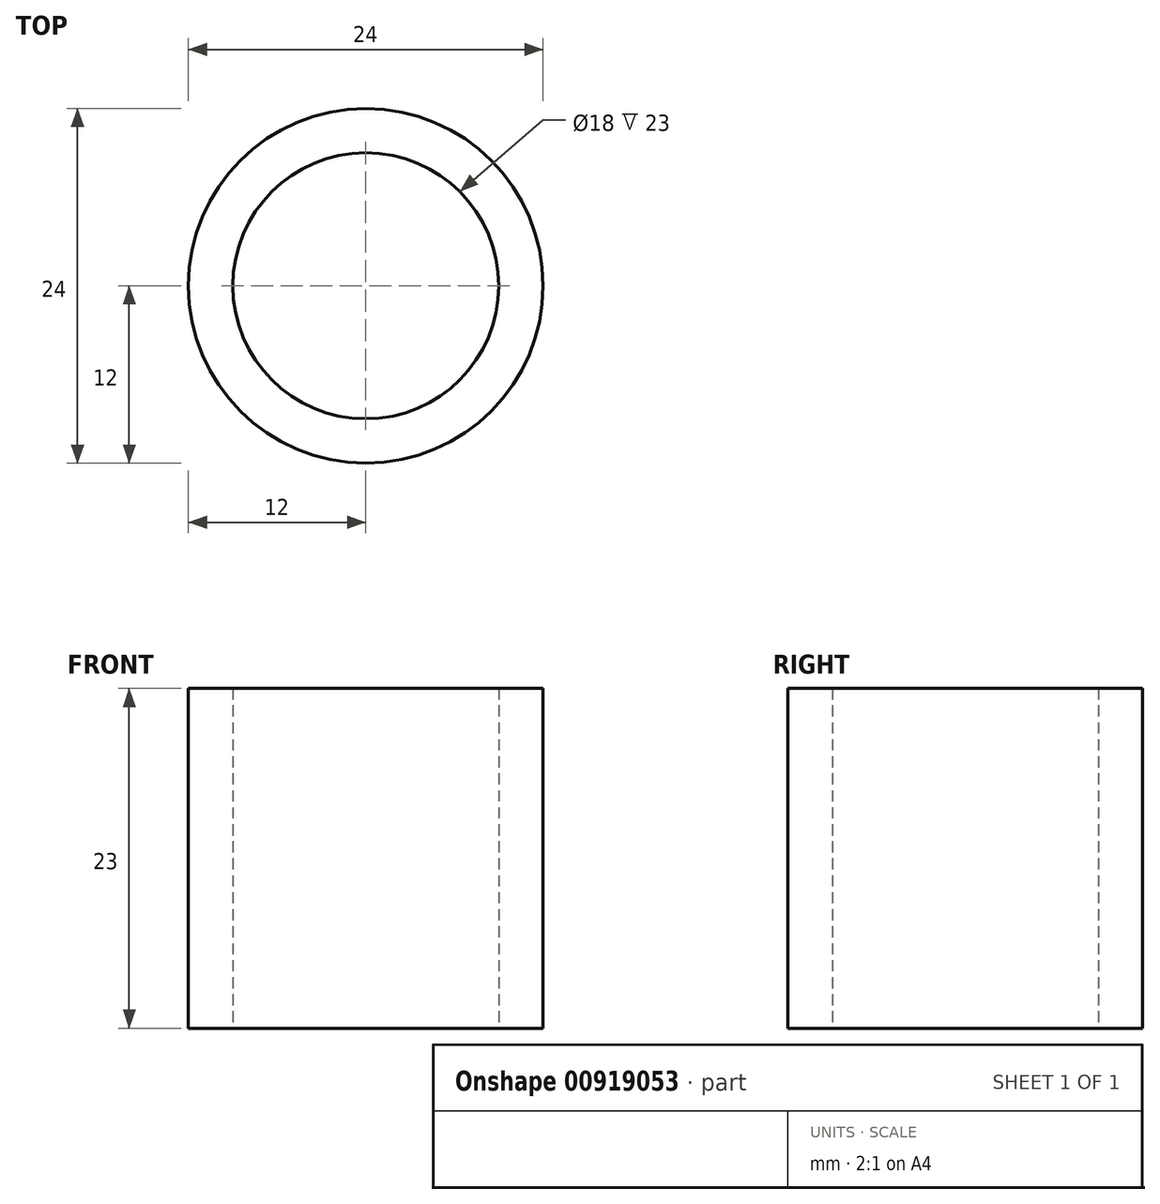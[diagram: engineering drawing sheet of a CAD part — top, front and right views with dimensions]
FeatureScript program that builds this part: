
annotation { "Feature Type Name" : "Feature", "Feature Type Description" : "" }
export const myFeature = defineFeature(function(context is Context, id is Id, definition is map)
    precondition{}
    {
        {
            var Q0;
            Q0=qCreatedBy(makeId("Top.planeOp"),FACE);
            var sketch = newSketch(context, id + "F0", { "sketchPlane" : qUnion([Q0])});
            skCircle(sketch, "E0", {"center": v(0, 0) * mm, "radius": 12 * mm});
            skSolve(sketch);
        }
        {
            var Q0;
            Q0=makeQuery(id+"F0.imprint","IMPRINT",FACE,{"disambiguationData":[TD([[makeQuery(id+"F0.imprint","IMPRINT",EDGE,{"derivedFrom":sQuery(id+"F0.wireOp",EDGE,"E0")}),1.0]])]});
            extrude(context, id + "F1", {"entities" : qUnion([Q0]), "depth" : 23 * mm, "offsetDistance" : 25 * mm});
        }
        {
            var Q0;
            Q0=qCreatedBy(makeId("Top.planeOp"),FACE);
            var sketch = newSketch(context, id + "F2", { "sketchPlane" : qUnion([Q0])});
            skCircle(sketch, "E1", {"center": v(0, 0) * mm, "radius": 9 * mm});
            skSolve(sketch);
        }
        {
            var Q0;
            Q0=sQuery(id+"F2.wireOp",VERTEX,"E1.center");
            var Q1;
            Q1=makeQuery(id+"F1.opExtrude","SWEPT_BODY",BODY,{"disambiguationData":[OSD([sQuery(id+"F0.wireOp",EDGE,"E0")])]});
            hole(context, id + "F3", {"style" : HoleStyle.SIMPLE, "endStyle" : HoleEndStyle.BLIND, "oppositeDirection" : true, "holeDiameter" : 18 * mm, "majorDiameter" : 5 * mm, "holeDepth" : 50 * mm, "isTappedThrough" : true, "tappedDepth" : 12 * mm, "tapClearance" : 3, "locations" : qUnion([Q0]), "scope" : qUnion([Q1])});
        }
    });
